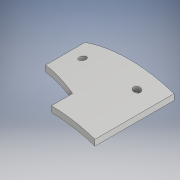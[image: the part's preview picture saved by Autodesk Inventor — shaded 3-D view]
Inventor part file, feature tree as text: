
AUTODESK INVENTOR PART (.ipt)
format: ipt  version: 2019 (Build 230136000, 136)  size: 144,896 bytes
history: native  units: mm
features: sketch x4, extrude x2, plane x2, hole x2, projected_geometry x1
ambient origin geometry x8: Origin, YZ Plane, XZ Plane, XY Plane, X Axis, Y Axis, Z Axis, Center Point
bodies: Solid1 (feature_tree)
feature tree (11):
  extrude  "Extrusion1"  Depth=70.0mm
  plane  "Work Plane1"
  hole  "Hole1"  [1 undecoded]
  plane  "Work Plane2"
  hole  "Hole2"  [1 undecoded]
  extrude  "Extrusion2"  Depth=10.0mm
  sketch  "Sketch1"  dims[d0=45.0mm d1=70.0mm]
  sketch  "Sketch2"  dims[d2=3.0mm d3=3.0mm]
  sketch  "Sketch3"  dims[d4=70.0mm d5=40.0mm d6=0.0mm]
  sketch  "Sketch4"  dims[d7=10.0mm d8=10.0mm d9=3.5mm d10=6.0mm d11=4.0mm d12=2.0mm d13=90.0deg d14=8.0mm d15=20.594885mm d16=10.0mm d17=10.0mm d18=3.5mm d19=6.0mm d20=4.0mm d21=2.0mm d22=90.0deg d23=8.0mm d24=20.594885mm d25=22.0mm d26=19.547688mm d27=20.0mm d28=0.0mm]
  projected_geometry  "Projected Loop1"
note: 2 required parameter values undecoded (feature->parameter linkage not recoverable at this tier; creation-order binding heuristic only, values carry confidence <= 0.55)
